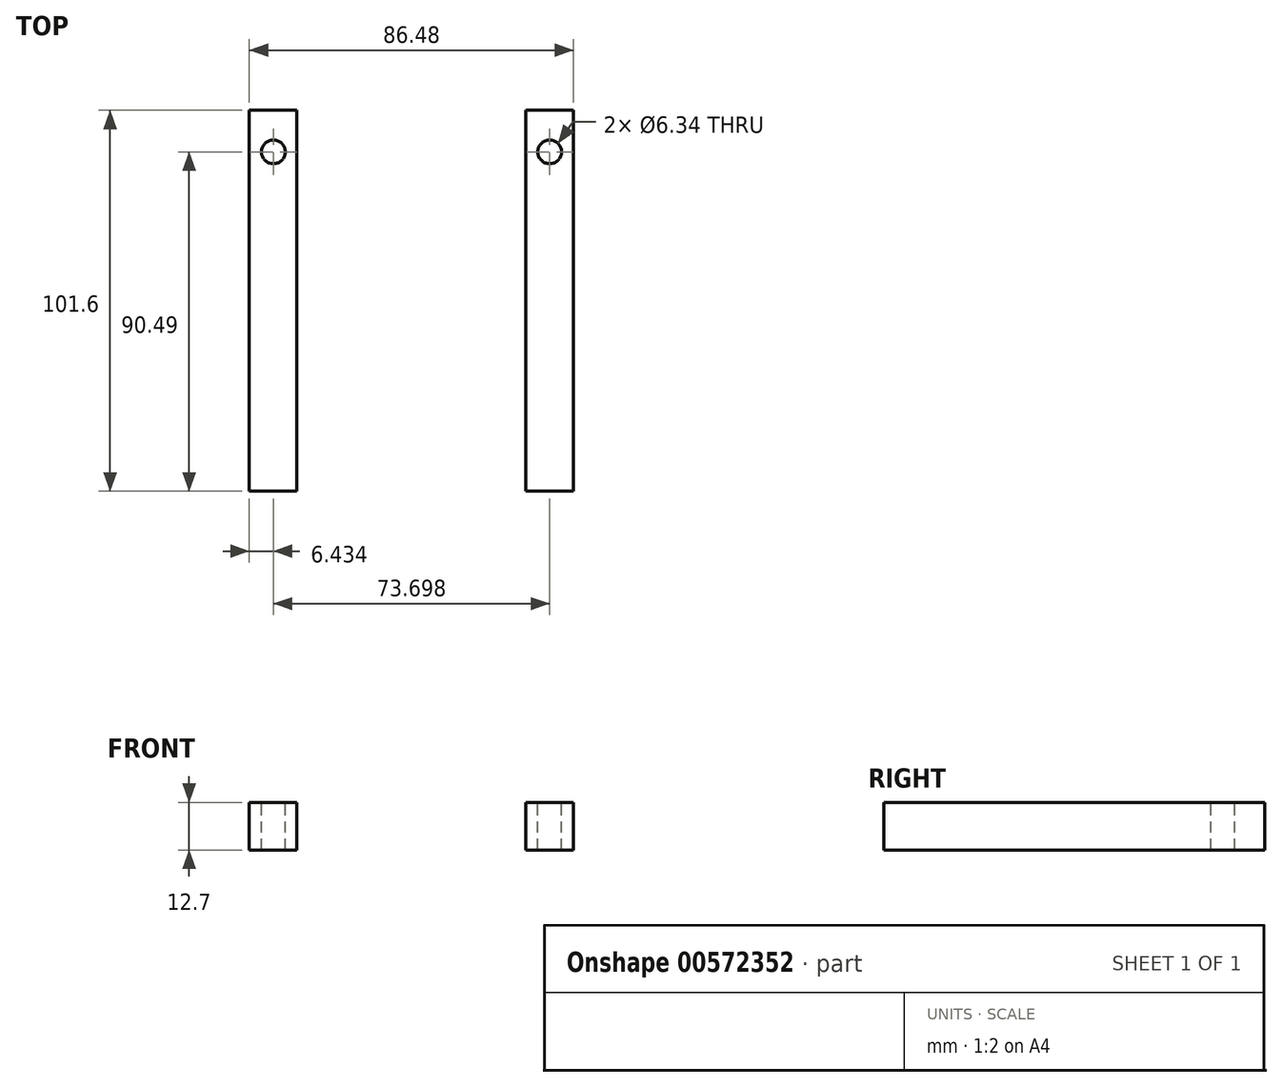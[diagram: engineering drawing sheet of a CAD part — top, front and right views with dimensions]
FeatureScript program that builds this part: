
annotation { "Feature Type Name" : "Feature", "Feature Type Description" : "" }
export const myFeature = defineFeature(function(context is Context, id is Id, definition is map)
    precondition{}
    {
        {
            var Q0;
            Q0=qCreatedBy(makeId("Top.planeOp"),FACE);
            var sketch = newSketch(context, id + "F0", { "sketchPlane" : qUnion([Q0])});
            skLineSegment(sketch, "E0.bottom", {"start": v(25.93, 31.21) * mm, "end": v(38.63, 31.21) * mm});
            skLineSegment(sketch, "E0.top", {"start": v(25.93, -70.39) * mm, "end": v(38.63, -70.39) * mm});
            skLineSegment(sketch, "E0.left", {"start": v(25.93, 31.21) * mm, "end": v(25.93, -70.39) * mm});
            skLineSegment(sketch, "E0.right", {"start": v(38.63, 31.21) * mm, "end": v(38.63, -70.39) * mm});
            skLineSegment(sketch, "E1.bottom", {"start": v(-47.85, 31.21) * mm, "end": v(-35.15, 31.21) * mm});
            skLineSegment(sketch, "E1.top", {"start": v(-47.85, -70.39) * mm, "end": v(-35.15, -70.39) * mm});
            skLineSegment(sketch, "E1.left", {"start": v(-47.85, 31.21) * mm, "end": v(-47.85, -70.39) * mm});
            skLineSegment(sketch, "E1.right", {"start": v(-35.15, 31.21) * mm, "end": v(-35.15, -70.39) * mm});
            skSolve(sketch);
        }
        {
            var Q0;
            Q0=makeQuery(id+"F0.imprint","IMPRINT",FACE,{"disambiguationData":[TD([[makeQuery(id+"F0.imprint","IMPRINT",EDGE,{"derivedFrom":sQuery(id+"F0.wireOp",EDGE,"E1.bottom")}),-1.0]])]});
            var Q1;
            Q1=makeQuery(id+"F0.imprint","IMPRINT",FACE,{"disambiguationData":[TD([[makeQuery(id+"F0.imprint","IMPRINT",EDGE,{"derivedFrom":sQuery(id+"F0.wireOp",EDGE,"E0.bottom")}),-1.0]])]});
            extrude(context, id + "F1", {"entities" : qUnion([Q0, Q1]), "depth" : 12.7 * mm, "offsetDistance" : 25.4 * mm});
        }
        {
            var Q0;
            Q0=makeQuery(id+"F1.opExtrude","CAP_FACE",FACE,{"disambiguationData":[OSD([sQuery(id+"F0.wireOp",EDGE,"E0.bottom"),sQuery(id+"F0.wireOp",EDGE,"E0.top"),sQuery(id+"F0.wireOp",EDGE,"E0.left"),sQuery(id+"F0.wireOp",EDGE,"E0.right")])],"isStart":false});
            var sketch = newSketch(context, id + "F2", { "sketchPlane" : qUnion([Q0])});
            skCircle(sketch, "E2", {"center": v(32.28, 20.1) * mm, "radius": 3.92 * mm});
            skPoint(sketch, "E2.centerSnap0", {"position": v(32.28, 31.21) * mm});
            skLineSegment(sketch, "E3", {"start": v(32.28, 20.1) * mm, "end": v(-41.42, 20.1) * mm});
            skSolve(sketch);
        }
        {
            var Q0;
            Q0=sQuery(id+"F2.wireOp",VERTEX,"E2.center");
            var Q1;
            Q1=makeQuery(id+"F1.opExtrude","SWEPT_BODY",BODY,{"disambiguationData":[OSD([sQuery(id+"F0.wireOp",EDGE,"E0.bottom"),sQuery(id+"F0.wireOp",EDGE,"E0.top"),sQuery(id+"F0.wireOp",EDGE,"E0.left"),sQuery(id+"F0.wireOp",EDGE,"E0.right")])]});
            hole(context, id + "F3", {"style" : HoleStyle.SIMPLE, "endStyle" : HoleEndStyle.THROUGH, "holeDiameter" : 6.34 * mm, "isTappedThrough" : true, "tappedDepth" : 12.7 * mm, "tapClearance" : 3, "locations" : qUnion([Q0]), "scope" : qUnion([Q1])});
        }
        {
            var Q0;
            Q0=sQuery(id+"F2.wireOp",VERTEX,"E3.end");
            var Q1;
            Q1=makeQuery(id+"F1.opExtrude","SWEPT_BODY",BODY,{"disambiguationData":[OSD([sQuery(id+"F0.wireOp",EDGE,"E1.bottom"),sQuery(id+"F0.wireOp",EDGE,"E1.top"),sQuery(id+"F0.wireOp",EDGE,"E1.left"),sQuery(id+"F0.wireOp",EDGE,"E1.right")])]});
            hole(context, id + "F4", {"style" : HoleStyle.SIMPLE, "endStyle" : HoleEndStyle.THROUGH, "holeDiameter" : 6.34 * mm, "isTappedThrough" : true, "tappedDepth" : 12.7 * mm, "tapClearance" : 3, "locations" : qUnion([Q0]), "scope" : qUnion([Q1])});
        }
    });
